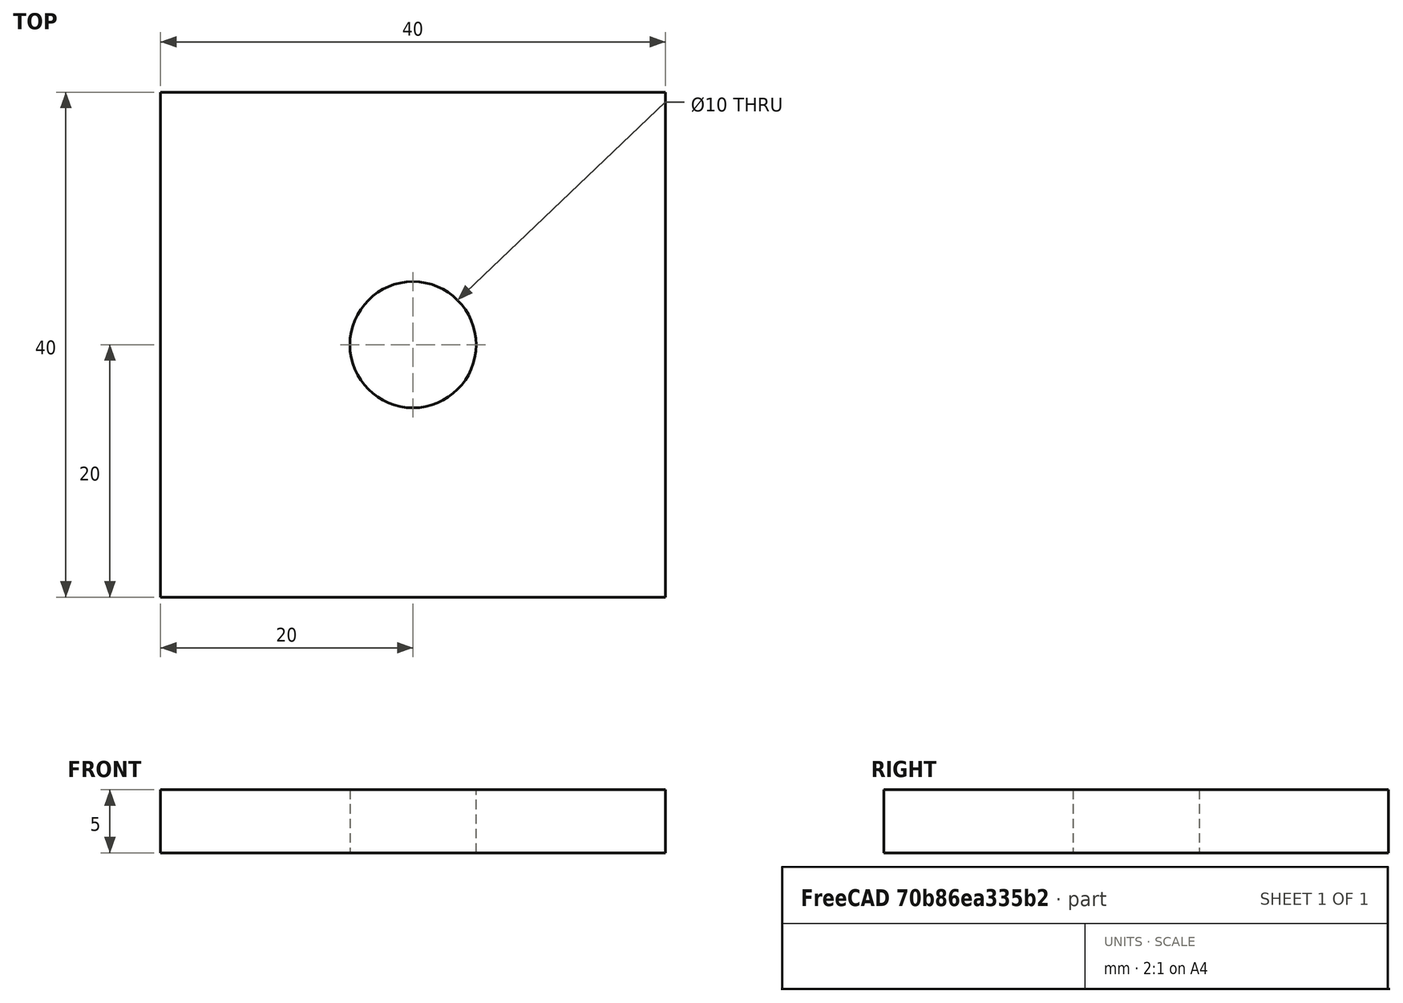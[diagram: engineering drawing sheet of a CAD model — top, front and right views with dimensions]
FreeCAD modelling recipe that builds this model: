
FCSTD DOCUMENT  (FreeCAD 0.20R29177 +233 (Git))
Label: pieza_sketch
License: Creative Commons Attribution-ShareAlike
LicenseURL: http://creativecommons.org/licenses/by-sa/4.0/
objects: Sketcher::SketchObject×1, Part::Extrusion×1
note: 2 computed .brp shape members not serialized (recipe doc carries the construction recipe); baked Part::Feature solids carry a one-line shape summary decoded from their .brp

FEATURE [Sketcher::SketchObject] Sketch
  FullyConstrained = true
  sketch-geometry (5):
    g0: LineSegment StartX=20 StartY=20 StartZ=0 EndX=-20 EndY=20 EndZ=0
    g1: LineSegment StartX=-20 StartY=20 StartZ=0 EndX=-20 EndY=-20 EndZ=0
    g2: LineSegment StartX=-20 StartY=-20 StartZ=0 EndX=20 EndY=-20 EndZ=0
    g3: LineSegment StartX=20 StartY=-20 StartZ=0 EndX=20 EndY=20 EndZ=0
    g4: Circle CenterX=0 CenterY=0 CenterZ=0 NormalX=0 NormalY=0 NormalZ=1 AngleXU=0 Radius=5
  constraints (13):
    c: Coincident(g0,g1)
    c: Coincident(g1,g2)
    c: Coincident(g2,g3)
    c: Coincident(g3,g0)
    c: Horizontal(g0)
    c: Horizontal(g2)
    c: Vertical(g1)
    c: Vertical(g3)
    c: Symmetric(g0,g1,g-1)
    c: Equal(g0,g3)
    c: DistanceX(g0,g0) = 40  'lado'
    c: Coincident(g4,g-1)
    c: Diameter(g4) = 10  'daimetro_taladro'
FEATURE [Part::Extrusion] Extrude
  Base = -> Sketch
  Dir = (0,0,1)
  DirMode = 2
  FaceMakerClass = Part::FaceMakerBullseye
  LengthFwd = 5
  LengthRev = 0
  Solid = true
  Symmetric = false
